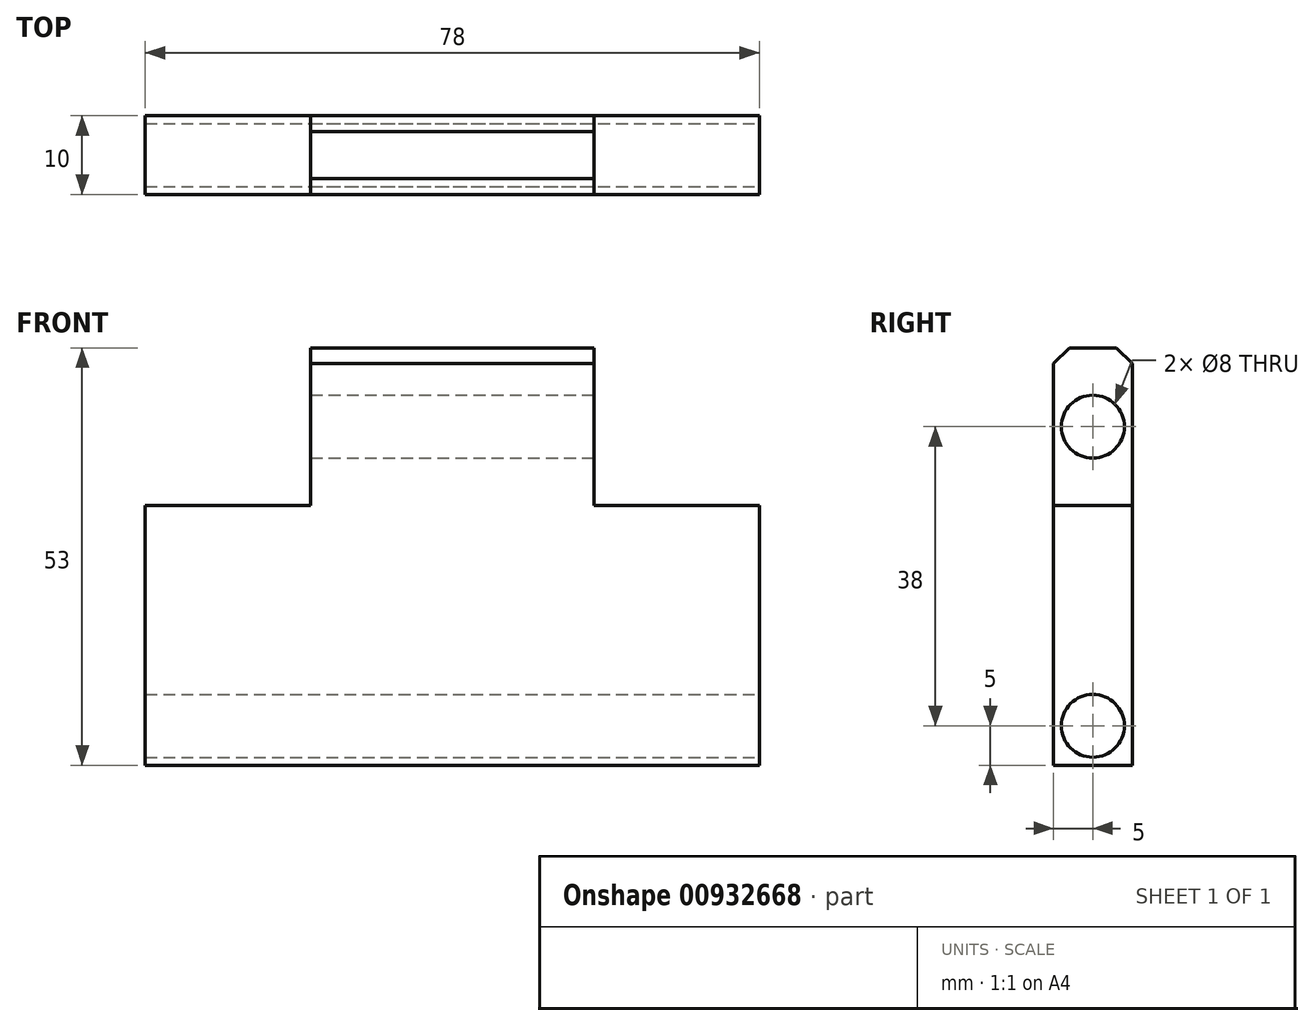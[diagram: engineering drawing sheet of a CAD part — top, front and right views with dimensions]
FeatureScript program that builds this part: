
annotation { "Feature Type Name" : "Feature", "Feature Type Description" : "" }
export const myFeature = defineFeature(function(context is Context, id is Id, definition is map)
    precondition{}
    {
        {
            var Q0;
            Q0=qCreatedBy(makeId("Front.planeOp"),FACE);
            var sketch = newSketch(context, id + "F0", { "sketchPlane" : qUnion([Q0])});
            skLineSegment(sketch, "E0.bottom", {"start": v(-19, 24) * mm, "end": v(19, 24) * mm});
            skLineSegment(sketch, "E0.top", {"start": v(-35, -24) * mm, "end": v(35, -24) * mm});
            skLineSegment(sketch, "E0.left", {"start": v(-35, 9) * mm, "end": v(-35, -24) * mm});
            skLineSegment(sketch, "E0.right", {"start": v(35, 9) * mm, "end": v(35, -24) * mm});
            skPoint(sketch, "E0.middle", {"position": v(0, 0) * mm});
            skLineSegment(sketch, "E1.left", {"start": v(19, 9) * mm, "end": v(19, 24) * mm});
            skLineSegment(sketch, "E1.right", {"start": v(-19, 9) * mm, "end": v(-19, 24) * mm});
            skPoint(sketch, "E1.middle", {"position": v(0, 24) * mm});
            skPoint(sketch, "E1.top.end.orphan", {"position": v(-19, 39) * mm});
            skPoint(sketch, "E2.orphan", {"position": v(19, 39) * mm});
            skLineSegment(sketch, "E3", {"start": v(-19, 9) * mm, "end": v(-35, 9) * mm});
            skLineSegment(sketch, "E4", {"start": v(-35, 9) * mm, "end": v(-19, 9) * mm});
            skPoint(sketch, "E5.orphan", {"position": v(-35, 24) * mm});
            skLineSegment(sketch, "E6", {"start": v(19, 9) * mm, "end": v(35, 9) * mm});
            skPoint(sketch, "E7.orphan", {"position": v(35, 24) * mm});
            skSolve(sketch);
        }
        {
            var Q0;
            Q0=makeQuery(id+"F0.imprint","IMPRINT",FACE,{"disambiguationData":[TD([[makeQuery(id+"F0.imprint","IMPRINT",EDGE,{"derivedFrom":sQuery(id+"F0.wireOp",EDGE,"E0.bottom")}),-1.0]])]});
            extrude(context, id + "F1", {"entities" : qUnion([Q0]), "depth" : 10 * mm, "offsetDistance" : 25 * mm});
        }
        {
            var Q0;
            Q0=makeQuery(id+"F1.opExtrude","SWEPT_FACE",FACE,{"disambiguationData":[OSD([sQuery(id+"F0.wireOp",EDGE,"E1.left")])]});
            var sketch = newSketch(context, id + "F2", { "sketchPlane" : qUnion([Q0])});
            skCircle(sketch, "E8", {"center": v(-5, 19) * mm, "radius": 4 * mm});
            skPoint(sketch, "E8.centerSnap0", {"position": v(-5, 24) * mm});
            skSolve(sketch);
        }
        {
            var Q0;
            Q0=qSketchRegion(id+"F2",true);
            extrude(context, id + "F3", {"entities" : qUnion([Q0]), "operationType" : NewBodyOperationType.REMOVE, "oppositeDirection" : true, "depth" : 38 * mm, "offsetDistance" : 25 * mm});
        }
        {
            var Q0;
            Q0=makeQuery(id+"F1.opExtrude","SWEPT_FACE",FACE,{"disambiguationData":[OSD([sQuery(id+"F0.wireOp",EDGE,"E0.right")])]});
            var sketch = newSketch(context, id + "F4", { "sketchPlane" : qUnion([Q0])});
            skCircle(sketch, "E9", {"center": v(-5, -19) * mm, "radius": 4 * mm});
            skPoint(sketch, "E9.centerSnap0", {"position": v(-5, -24) * mm});
            skSolve(sketch);
        }
        {
            var Q0;
            Q0=makeQuery(id+"F4.imprint","IMPRINT",FACE,{"disambiguationData":[TD([[makeQuery(id+"F4.imprint","IMPRINT",EDGE,{"derivedFrom":sQuery(id+"F4.wireOp",EDGE,"E9")}),1.0]])]});
            extrude(context, id + "F5", {"entities" : qUnion([Q0]), "operationType" : NewBodyOperationType.REMOVE, "oppositeDirection" : true, "depth" : 70 * mm, "offsetDistance" : 25 * mm});
        }
        {
            var Q0;
            Q0=makeQuery(id+"F1.opExtrude","SWEPT_BODY",BODY,{"disambiguationData":[OSD([sQuery(id+"F0.wireOp",EDGE,"E0.bottom"),sQuery(id+"F0.wireOp",EDGE,"E0.top"),sQuery(id+"F0.wireOp",EDGE,"E0.left"),sQuery(id+"F0.wireOp",EDGE,"E0.right"),sQuery(id+"F0.wireOp",EDGE,"E1.left"),sQuery(id+"F0.wireOp",EDGE,"E1.right"),sQuery(id+"F0.wireOp",EDGE,"E4"),sQuery(id+"F0.wireOp",EDGE,"E6")])]});
            deleteBodies(context, id + "F6", {"entities" : qUnion([Q0])});
        }
        {
            var Q0;
            Q0=qCreatedBy(makeId("Front.planeOp"),FACE);
            var sketch = newSketch(context, id + "F7", { "sketchPlane" : qUnion([Q0])});
            skLineSegment(sketch, "E10.bottom", {"start": v(-18, 24) * mm, "end": v(18, 24) * mm});
            skLineSegment(sketch, "E10.top", {"start": v(-39, -24) * mm, "end": v(39, -24) * mm});
            skLineSegment(sketch, "E10.left", {"start": v(-39, 9) * mm, "end": v(-39, -24) * mm});
            skLineSegment(sketch, "E10.right", {"start": v(39, 9) * mm, "end": v(39, -24) * mm});
            skPoint(sketch, "E10.middle", {"position": v(0, 0) * mm});
            skLineSegment(sketch, "E11.top", {"start": v(-39, 9) * mm, "end": v(-18, 9) * mm});
            skLineSegment(sketch, "E11.right", {"start": v(-18, 24) * mm, "end": v(-18, 9) * mm});
            skLineSegment(sketch, "E12.top", {"start": v(39, 9) * mm, "end": v(18, 9) * mm});
            skLineSegment(sketch, "E12.right", {"start": v(18, 24) * mm, "end": v(18, 9) * mm});
            skSolve(sketch);
        }
        {
            var Q0;
            Q0=qSketchRegion(id+"F7",true);
            var Q1;
            Q1=makeQuery(id+"F7.imprint","IMPRINT",FACE,{"disambiguationData":[TD([[makeQuery(id+"F7.imprint","IMPRINT",EDGE,{"derivedFrom":sQuery(id+"F7.wireOp",EDGE,"E10.bottom")}),-1.0]])]});
            extrude(context, id + "F8", {"entities" : qUnion([Q0, Q1]), "depth" : 10 * mm, "offsetDistance" : 25 * mm});
        }
        {
            var Q0;
            Q0=makeQuery(id+"F8.opExtrude","SWEPT_FACE",FACE,{"disambiguationData":[OSD([sQuery(id+"F7.wireOp",EDGE,"E12.right")])]});
            var sketch = newSketch(context, id + "F9", { "sketchPlane" : qUnion([Q0])});
            skCircle(sketch, "E13", {"center": v(-5, 19) * mm, "radius": 4 * mm});
            skPoint(sketch, "E13.centerSnap0", {"position": v(-5, 24) * mm});
            skSolve(sketch);
        }
        {
            var Q0;
            Q0=qSketchRegion(id+"F9",true);
            extrude(context, id + "F10", {"entities" : qUnion([Q0]), "operationType" : NewBodyOperationType.REMOVE, "oppositeDirection" : true, "depth" : 40 * mm, "offsetDistance" : 25 * mm});
        }
        {
            var Q0;
            Q0=makeQuery(id+"F8.opExtrude","SWEPT_FACE",FACE,{"disambiguationData":[OSD([sQuery(id+"F7.wireOp",EDGE,"E10.right")])]});
            var sketch = newSketch(context, id + "F11", { "sketchPlane" : qUnion([Q0])});
            skCircle(sketch, "E14", {"center": v(-5, -19) * mm, "radius": 4 * mm});
            skPoint(sketch, "E14.centerSnap0", {"position": v(-5, -24) * mm});
            skSolve(sketch);
        }
        {
            var Q0;
            Q0=qSketchRegion(id+"F11",true);
            extrude(context, id + "F12", {"entities" : qUnion([Q0]), "operationType" : NewBodyOperationType.REMOVE, "oppositeDirection" : true, "depth" : 100 * mm, "offsetDistance" : 25 * mm});
        }
        {
            var Q0;
            Q0=makeQuery(id+"F8.opExtrude","SWEPT_FACE",FACE,{"disambiguationData":[OSD([sQuery(id+"F7.wireOp",EDGE,"E10.bottom")])]});
            extrude(context, id + "F13", {"entities" : qUnion([Q0]), "operationType" : NewBodyOperationType.ADD, "depth" : 5 * mm, "offsetDistance" : 25 * mm});
        }
        {
            var Q0;
            {var subQ0=sQuery(id+"F7.wireOp",EDGE,"E10.bottom");Q0=makeQuery(id+"F13.opExtrude","CAP_EDGE",EDGE,{"disambiguationData":[OSD([subQ0]),TDD([makeQuery(id+"F8.opExtrude","CAP_EDGE",EDGE,{"disambiguationData":[OSD([subQ0])],"isStart":false})])],"isStart":false});}
            var Q1;
            {var subQ0=sQuery(id+"F7.wireOp",EDGE,"E10.bottom");Q1=makeQuery(id+"F13.opExtrude","CAP_EDGE",EDGE,{"disambiguationData":[OSD([subQ0]),TDD([makeQuery(id+"F8.opExtrude","CAP_EDGE",EDGE,{"disambiguationData":[OSD([subQ0])],"isStart":true})])],"isStart":false});}
            chamfer(context, id + "F14", {"entities" : qUnion([Q0, Q1]), "width" : 2 * mm, "tangentPropagation" : true});
        }
    });
